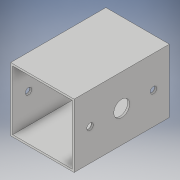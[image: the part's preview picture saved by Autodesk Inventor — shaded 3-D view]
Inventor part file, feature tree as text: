
AUTODESK INVENTOR PART (.ipt)
format: ipt  version: 2018 (Build 220112000, 112)  size: 126,464 bytes
history: native  units: in
note: dims shown in document units (in); Inventor stores cm internally (conversion verified against a paired STEP export)
features: extrude x4, sketch x4
ambient origin geometry x8: Origin, YZ Plane, XZ Plane, XY Plane, X Axis, Y Axis, Z Axis, Center Point
bodies: Solid1 (feature_tree)
feature tree (8):
  extrude  "Extrusion1"  Depth=2.0in
  extrude  "Extrusion2"  Depth=3.0in TaperAngle=0.0deg
  extrude  "Extrusion3"  Depth=0.1875in TaperAngle=0.0deg
  extrude  "Extrusion4"  Depth=2.0in TaperAngle=0.0deg
  sketch  "Sketch1"  dims[d0=2.0in d1=2.0in]
  sketch  "Sketch2"  dims[d2=0.0625in d3=3.0in d4=0.0in]
  sketch  "Sketch3"  dims[d5=0.5in d6=0.1875in d7=0.0in]
  sketch  "Sketch4"  dims[d8=0.5in d9=0.1875in d10=0.0in d11=0.5in d12=2.0in d13=0.2031in d14=2.1875in d15=0.0in d16=1.5in d17=1.0in]
